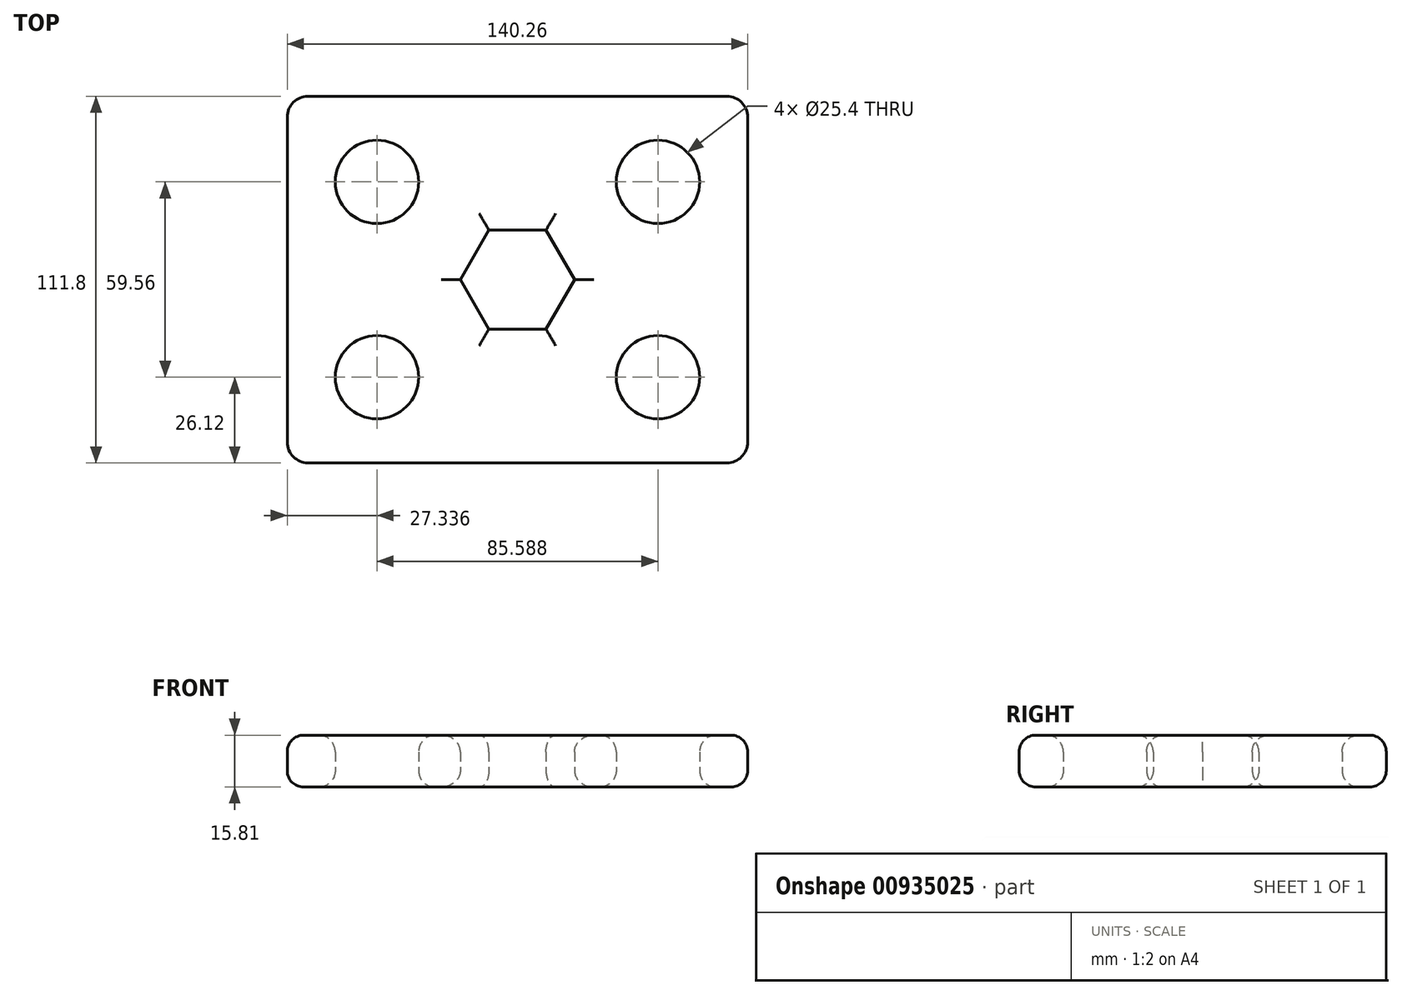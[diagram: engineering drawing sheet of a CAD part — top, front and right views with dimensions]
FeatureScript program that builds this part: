
annotation { "Feature Type Name" : "Feature", "Feature Type Description" : "" }
export const myFeature = defineFeature(function(context is Context, id is Id, definition is map)
    precondition{}
    {
        {
            var Q0;
            Q0=qCreatedBy(makeId("Top.planeOp"),FACE);
            var sketch = newSketch(context, id + "F0", { "sketchPlane" : qUnion([Q0])});
            skPoint(sketch, "E0.middle", {"position": v(0, 0) * mm});
            skCircle(sketch, "E1", {"center": v(42.8, 29.78) * mm, "radius": 12.7 * mm});
            skCircle(sketch, "E2", {"center": v(42.8, -29.78) * mm, "radius": 12.7 * mm});
            skCircle(sketch, "E3", {"center": v(-42.8, 29.78) * mm, "radius": 12.7 * mm});
            skCircle(sketch, "E4", {"center": v(-42.8, -29.78) * mm, "radius": 12.7 * mm});
            skLineSegment(sketch, "E5.bottom", {"start": v(63.78, -55.9) * mm, "end": v(-63.78, -55.9) * mm});
            skLineSegment(sketch, "E5.top", {"start": v(63.78, 55.9) * mm, "end": v(-63.78, 55.9) * mm});
            skLineSegment(sketch, "E5.left", {"start": v(70.13, -49.55) * mm, "end": v(70.13, 49.55) * mm});
            skLineSegment(sketch, "E5.right", {"start": v(-70.13, -49.55) * mm, "end": v(-70.13, 49.55) * mm});
            skCircle(sketch, "E6.cCircle", {"center": v(0, 0) * mm, "radius": 17.4 * mm, "construction": true});
            skLineSegment(sketch, "E6.0", {"start": v(17.4, 0) * mm, "end": v(8.7, -15.07) * mm});
            skLineSegment(sketch, "E6.1", {"start": v(8.7, -15.07) * mm, "end": v(-8.7, -15.07) * mm});
            skLineSegment(sketch, "E6.2", {"start": v(-8.7, -15.07) * mm, "end": v(-17.4, 0) * mm});
            skLineSegment(sketch, "E6.3", {"start": v(-17.4, 0) * mm, "end": v(-8.7, 15.07) * mm});
            skLineSegment(sketch, "E6.4", {"start": v(-8.7, 15.07) * mm, "end": v(8.7, 15.07) * mm});
            skLineSegment(sketch, "E6.5", {"start": v(8.7, 15.07) * mm, "end": v(17.4, 0) * mm});
            skPoint(sketch, "E7.visualSharp", {"position": v(-70.13, 55.9) * mm});
            skArc(sketch, "E7.filletArc", {"start": v(-63.78, 55.9) * mm, "mid": v(-68.27, 54.04) * mm, "end": v(-70.13, 49.55) * mm});
            skPoint(sketch, "E8.visualSharp", {"position": v(-70.13, -55.9) * mm});
            skArc(sketch, "E8.filletArc", {"start": v(-70.13, -49.55) * mm, "mid": v(-68.27, -54.04) * mm, "end": v(-63.78, -55.9) * mm});
            skPoint(sketch, "E9.visualSharp", {"position": v(70.13, -55.9) * mm});
            skArc(sketch, "E9.filletArc", {"start": v(63.78, -55.9) * mm, "mid": v(68.27, -54.04) * mm, "end": v(70.13, -49.55) * mm});
            skPoint(sketch, "E10.visualSharp", {"position": v(70.13, 55.9) * mm});
            skArc(sketch, "E10.filletArc", {"start": v(70.13, 49.55) * mm, "mid": v(68.27, 54.04) * mm, "end": v(63.78, 55.9) * mm});
            skSolve(sketch);
        }
        {
            var Q0;
            Q0=makeQuery(id+"F0.imprint","IMPRINT",FACE,{"disambiguationData":[TD([[makeQuery(id+"F0.imprint","IMPRINT",EDGE,{"derivedFrom":sQuery(id+"F0.wireOp",EDGE,"E3")}),1.0]])]});
            var Q1;
            Q1=makeQuery(id+"F0.imprint","IMPRINT",FACE,{"disambiguationData":[TD([[makeQuery(id+"F0.imprint","IMPRINT",EDGE,{"derivedFrom":sQuery(id+"F0.wireOp",EDGE,"E4")}),1.0]])]});
            var Q2;
            Q2=makeQuery(id+"F0.imprint","IMPRINT",FACE,{"disambiguationData":[TD([[makeQuery(id+"F0.imprint","IMPRINT",EDGE,{"derivedFrom":sQuery(id+"F0.wireOp",EDGE,"E6.0")}),-1.0]])]});
            var Q3;
            Q3=makeQuery(id+"F0.imprint","IMPRINT",FACE,{"disambiguationData":[TD([[makeQuery(id+"F0.imprint","IMPRINT",EDGE,{"derivedFrom":sQuery(id+"F0.wireOp",EDGE,"E2")}),1.0]])]});
            var Q4;
            Q4=makeQuery(id+"F0.imprint","IMPRINT",FACE,{"disambiguationData":[TD([[makeQuery(id+"F0.imprint","IMPRINT",EDGE,{"derivedFrom":sQuery(id+"F0.wireOp",EDGE,"E1")}),1.0]])]});
            extrude(context, id + "F1", {"entities" : qUnion([Q0, Q1, Q2, Q3, Q4]), "depth" : 25.4 * mm, "offsetDistance" : 25.4 * mm});
        }
        {
            var Q0;
            Q0=makeQuery(id+"F0.imprint","IMPRINT",FACE,{"disambiguationData":[TD([[makeQuery(id+"F0.imprint","IMPRINT",EDGE,{"derivedFrom":sQuery(id+"F0.wireOp",EDGE,"E1")}),-1.0]])]});
            extrude(context, id + "F2", {"entities" : qUnion([Q0]), "depth" : 15.8 * mm, "offsetDistance" : 25.4 * mm});
        }
        {
            var Q0;
            Q0=makeQuery(id+"F1.opExtrude","SWEPT_BODY",BODY,{"disambiguationData":[OSD([sQuery(id+"F0.wireOp",EDGE,"E1")])]});
            var Q1;
            Q1=makeQuery(id+"F1.opExtrude","SWEPT_BODY",BODY,{"disambiguationData":[OSD([sQuery(id+"F0.wireOp",EDGE,"E2")])]});
            var Q2;
            Q2=makeQuery(id+"F1.opExtrude","SWEPT_BODY",BODY,{"disambiguationData":[OSD([sQuery(id+"F0.wireOp",EDGE,"E3")])]});
            var Q3;
            Q3=makeQuery(id+"F1.opExtrude","SWEPT_BODY",BODY,{"disambiguationData":[OSD([sQuery(id+"F0.wireOp",EDGE,"E4")])]});
            var Q4;
            Q4=makeQuery(id+"F2.opExtrude","SWEPT_BODY",BODY,{"disambiguationData":[OSD([sQuery(id+"F0.wireOp",EDGE,"E1"),sQuery(id+"F0.wireOp",EDGE,"E2"),sQuery(id+"F0.wireOp",EDGE,"E3"),sQuery(id+"F0.wireOp",EDGE,"E4"),sQuery(id+"F0.wireOp",EDGE,"E5.bottom"),sQuery(id+"F0.wireOp",EDGE,"E5.top"),sQuery(id+"F0.wireOp",EDGE,"E5.left"),sQuery(id+"F0.wireOp",EDGE,"E5.right"),sQuery(id+"F0.wireOp",EDGE,"E6.0"),sQuery(id+"F0.wireOp",EDGE,"E6.1"),sQuery(id+"F0.wireOp",EDGE,"E6.2"),sQuery(id+"F0.wireOp",EDGE,"E6.3"),sQuery(id+"F0.wireOp",EDGE,"E6.4"),sQuery(id+"F0.wireOp",EDGE,"E6.5"),sQuery(id+"F0.wireOp",EDGE,"E7.filletArc"),sQuery(id+"F0.wireOp",EDGE,"E8.filletArc"),sQuery(id+"F0.wireOp",EDGE,"E9.filletArc"),sQuery(id+"F0.wireOp",EDGE,"E10.filletArc")])]});
            booleanBodies(context, id + "F3", {"operationType" : BooleanOperationType.SUBTRACTION, "tools" : qUnion([Q0, Q1, Q2, Q3]), "targets" : qUnion([Q4])});
        }
        {
            var Q0;
            Q0=makeQuery(id+"F1.opExtrude","SWEPT_BODY",BODY,{"disambiguationData":[OSD([sQuery(id+"F0.wireOp",EDGE,"E6.0"),sQuery(id+"F0.wireOp",EDGE,"E6.1"),sQuery(id+"F0.wireOp",EDGE,"E6.2"),sQuery(id+"F0.wireOp",EDGE,"E6.3"),sQuery(id+"F0.wireOp",EDGE,"E6.4"),sQuery(id+"F0.wireOp",EDGE,"E6.5")])]});
            var Q1;
            Q1=makeQuery(id+"F2.opExtrude","SWEPT_BODY",BODY,{"disambiguationData":[OSD([sQuery(id+"F0.wireOp",EDGE,"E1"),sQuery(id+"F0.wireOp",EDGE,"E2"),sQuery(id+"F0.wireOp",EDGE,"E3"),sQuery(id+"F0.wireOp",EDGE,"E4"),sQuery(id+"F0.wireOp",EDGE,"E5.bottom"),sQuery(id+"F0.wireOp",EDGE,"E5.top"),sQuery(id+"F0.wireOp",EDGE,"E5.left"),sQuery(id+"F0.wireOp",EDGE,"E5.right"),sQuery(id+"F0.wireOp",EDGE,"E6.0"),sQuery(id+"F0.wireOp",EDGE,"E6.1"),sQuery(id+"F0.wireOp",EDGE,"E6.2"),sQuery(id+"F0.wireOp",EDGE,"E6.3"),sQuery(id+"F0.wireOp",EDGE,"E6.4"),sQuery(id+"F0.wireOp",EDGE,"E6.5"),sQuery(id+"F0.wireOp",EDGE,"E7.filletArc"),sQuery(id+"F0.wireOp",EDGE,"E8.filletArc"),sQuery(id+"F0.wireOp",EDGE,"E9.filletArc"),sQuery(id+"F0.wireOp",EDGE,"E10.filletArc")])]});
            booleanBodies(context, id + "F4", {"operationType" : BooleanOperationType.SUBTRACTION, "tools" : qUnion([Q0]), "targets" : qUnion([Q1])});
        }
        {
            var Q0;
            Q0=makeQuery(id+"F2.opExtrude","CAP_FACE",FACE,{"disambiguationData":[OSD([sQuery(id+"F0.wireOp",EDGE,"E1"),sQuery(id+"F0.wireOp",EDGE,"E2"),sQuery(id+"F0.wireOp",EDGE,"E3"),sQuery(id+"F0.wireOp",EDGE,"E4"),sQuery(id+"F0.wireOp",EDGE,"E5.bottom"),sQuery(id+"F0.wireOp",EDGE,"E5.top"),sQuery(id+"F0.wireOp",EDGE,"E5.left"),sQuery(id+"F0.wireOp",EDGE,"E5.right"),sQuery(id+"F0.wireOp",EDGE,"E6.0"),sQuery(id+"F0.wireOp",EDGE,"E6.1"),sQuery(id+"F0.wireOp",EDGE,"E6.2"),sQuery(id+"F0.wireOp",EDGE,"E6.3"),sQuery(id+"F0.wireOp",EDGE,"E6.4"),sQuery(id+"F0.wireOp",EDGE,"E6.5"),sQuery(id+"F0.wireOp",EDGE,"E7.filletArc"),sQuery(id+"F0.wireOp",EDGE,"E8.filletArc"),sQuery(id+"F0.wireOp",EDGE,"E9.filletArc"),sQuery(id+"F0.wireOp",EDGE,"E10.filletArc")])],"isStart":false});
            fillet(context, id + "F5", {"entities" : qUnion([Q0]), "radius" : 5.08 * mm, "tangentPropagation" : true, "allowEdgeOverflow" : false});
        }
        {
            var Q0;
            Q0 = qSketchRegion(id + "F0", true);
            var sketch = newSketch(context, id + "F6", { "sketchPlane" : qUnion([Q0])});
            skCircle(sketch, "E11", {"center": v(108.13, 28.08) * mm, "radius": 13.52 * mm});
            skSolve(sketch);
        }
        {
            var Q0;
            Q0 = qSketchRegion(id + "F6", true);
            var Q1;
            Q1=makeQuery(id+"F6.imprint","IMPRINT",FACE,{"disambiguationData":[TD([[makeQuery(id+"F6.imprint","IMPRINT",EDGE,{"derivedFrom":sQuery(id+"F6.wireOp",EDGE,"E11")}),1.0]])]});
            extrude(context, id + "F7", {"entities" : qUnion([Q0, Q1]), "depth" : 25 * mm, "offsetDistance" : 25 * mm});
        }
        {
            var Q0;
            Q0=makeQuery(id+"F7.opExtrude","CAP_FACE",FACE,{"disambiguationData":[OSD([sQuery(id+"F6.wireOp",EDGE,"E11")])],"isStart":false});
            var sketch = newSketch(context, id + "F8", { "sketchPlane" : qUnion([Q0])});
            skCircle(sketch, "E12.cCircle", {"center": v(108.13, 28.08) * mm, "radius": 13.52 * mm, "construction": true});
            skLineSegment(sketch, "E12.0", {"start": v(119.68, 21.05) * mm, "end": v(107.82, 14.56) * mm});
            skLineSegment(sketch, "E12.1", {"start": v(107.82, 14.56) * mm, "end": v(96.27, 21.59) * mm});
            skLineSegment(sketch, "E12.2", {"start": v(96.27, 21.59) * mm, "end": v(96.58, 35.1) * mm});
            skLineSegment(sketch, "E12.3", {"start": v(96.58, 35.1) * mm, "end": v(108.44, 41.6) * mm});
            skLineSegment(sketch, "E12.4", {"start": v(108.44, 41.6) * mm, "end": v(120, 34.57) * mm});
            skLineSegment(sketch, "E12.5", {"start": v(120, 34.57) * mm, "end": v(119.68, 21.05) * mm});
            skSolve(sketch);
        }
        {
            var Q0;
            Q0=makeQuery(id+"F8.imprint","IMPRINT",FACE,{"disambiguationData":[TD([[makeQuery(id+"F8.imprint","IMPRINT",EDGE,{"derivedFrom":sQuery(id+"F8.wireOp",EDGE,"E12.0")}),-1.0]])]});
            extrude(context, id + "F9", {"entities" : qUnion([Q0]), "operationType" : NewBodyOperationType.ADD, "depth" : 10.47 * mm, "offsetDistance" : 25 * mm});
        }
        {
            var Q0;
            Q0=makeQuery(id+"F9.opExtrude","CAP_FACE",FACE,{"disambiguationData":[OSD([sQuery(id+"F8.wireOp",EDGE,"E12.0"),sQuery(id+"F8.wireOp",EDGE,"E12.1"),sQuery(id+"F8.wireOp",EDGE,"E12.2"),sQuery(id+"F8.wireOp",EDGE,"E12.3"),sQuery(id+"F8.wireOp",EDGE,"E12.4"),sQuery(id+"F8.wireOp",EDGE,"E12.5")])],"isStart":false});
            var sketch = newSketch(context, id + "F10", { "sketchPlane" : qUnion([Q0])});
            skCircle(sketch, "E13", {"center": v(120, 34.57) * mm, "radius": 6.79 * mm});
            skSolve(sketch);
        }
        {
            var Q0;
            {var subQ0=sQuery(id+"F10.wireOp",EDGE,"E13");var subQ1=makeQuery(id+"F9.opExtrude","CAP_EDGE",EDGE,{"disambiguationData":[OSD([sQuery(id+"F8.wireOp",EDGE,"E12.4")])],"isStart":false});var subQ2=makeQuery(id+"F10.imprint","INTERSECT",VERTEX,{"derivedFrom":[subQ1,subQ0]});Q0=makeQuery(id+"F10.imprint","IMPRINT",FACE,{"disambiguationData":[TD([[makeQuery(id+"F10.imprint","IMPRINT",EDGE,{"disambiguationData":[TD([[subQ2,1.0]])],"derivedFrom":subQ0}),1.0]])]});}
            extrude(context, id + "F11", {"entities" : qUnion([Q0]), "operationType" : NewBodyOperationType.ADD, "oppositeDirection" : true, "depth" : 23.9 * mm, "offsetDistance" : 25 * mm});
        }
        {
            var Q0;
            Q0=makeQuery(id+"F7.opExtrude","SWEPT_BODY",BODY,{"disambiguationData":[OSD([sQuery(id+"F6.wireOp",EDGE,"E11")])]});
            deleteBodies(context, id + "F12", {"entities" : qUnion([Q0])});
        }
        {
            var Q0;
            Q0=makeQuery(id+"F2.opExtrude","CAP_FACE",FACE,{"disambiguationData":[OSD([sQuery(id+"F0.wireOp",EDGE,"E1"),sQuery(id+"F0.wireOp",EDGE,"E2"),sQuery(id+"F0.wireOp",EDGE,"E3"),sQuery(id+"F0.wireOp",EDGE,"E4"),sQuery(id+"F0.wireOp",EDGE,"E5.bottom"),sQuery(id+"F0.wireOp",EDGE,"E5.top"),sQuery(id+"F0.wireOp",EDGE,"E5.left"),sQuery(id+"F0.wireOp",EDGE,"E5.right"),sQuery(id+"F0.wireOp",EDGE,"E6.0"),sQuery(id+"F0.wireOp",EDGE,"E6.1"),sQuery(id+"F0.wireOp",EDGE,"E6.2"),sQuery(id+"F0.wireOp",EDGE,"E6.3"),sQuery(id+"F0.wireOp",EDGE,"E6.4"),sQuery(id+"F0.wireOp",EDGE,"E6.5"),sQuery(id+"F0.wireOp",EDGE,"E7.filletArc"),sQuery(id+"F0.wireOp",EDGE,"E8.filletArc"),sQuery(id+"F0.wireOp",EDGE,"E9.filletArc"),sQuery(id+"F0.wireOp",EDGE,"E10.filletArc")])],"isStart":true});
            fillet(context, id + "F13", {"entities" : qUnion([Q0]), "radius" : 5 * mm, "tangentPropagation" : true, "allowEdgeOverflow" : false});
        }
    });
